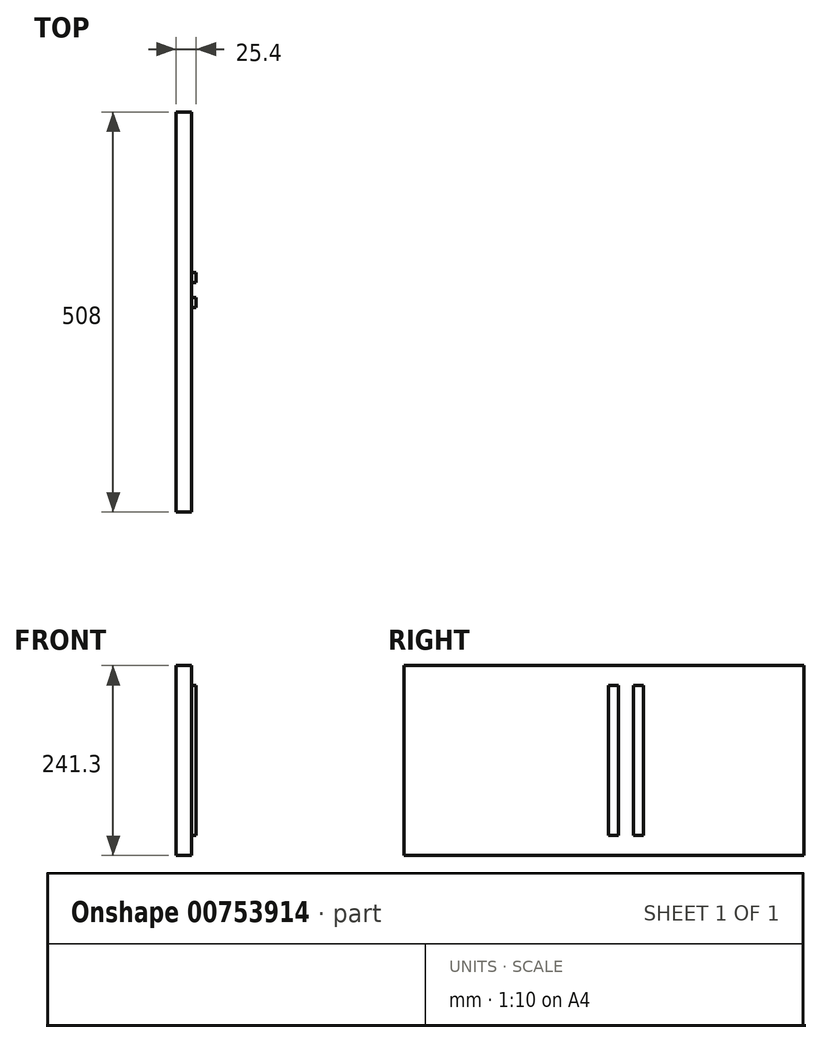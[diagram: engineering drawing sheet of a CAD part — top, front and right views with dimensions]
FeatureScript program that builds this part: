
annotation { "Feature Type Name" : "Feature", "Feature Type Description" : "" }
export const myFeature = defineFeature(function(context is Context, id is Id, definition is map)
    precondition{}
    {
        {
            var Q0;
            Q0=qCreatedBy(makeId("Right.planeOp"),FACE);
            var sketch = newSketch(context, id + "F0", { "sketchPlane" : qUnion([Q0])});
            skLineSegment(sketch, "E0.bottom", {"start": v(254, -120.65) * mm, "end": v(-254, -120.65) * mm});
            skLineSegment(sketch, "E0.top", {"start": v(254, 120.65) * mm, "end": v(-254, 120.65) * mm});
            skLineSegment(sketch, "E0.left", {"start": v(254, -120.65) * mm, "end": v(254, 120.65) * mm});
            skLineSegment(sketch, "E0.right", {"start": v(-254, -120.65) * mm, "end": v(-254, 120.65) * mm});
            skPoint(sketch, "E0.middle", {"position": v(0, 0) * mm});
            skLineSegment(sketch, "E1.0", {"start": v(253.65, 95.25) * mm, "end": v(-254, 95.25) * mm});
            skLineSegment(sketch, "E2.0", {"start": v(254, -95.25) * mm, "end": v(-254, -95.25) * mm});
            skLineSegment(sketch, "E3", {"start": v(253.65, 95.25) * mm, "end": v(50.45, 95.25) * mm});
            skLineSegment(sketch, "E4", {"start": v(50.45, 95.25) * mm, "end": v(37.75, 95.25) * mm});
            skLineSegment(sketch, "E5", {"start": v(37.75, 95.25) * mm, "end": v(18.7, 95.25) * mm});
            skLineSegment(sketch, "E6", {"start": v(18.7, 95.25) * mm, "end": v(6, 95.25) * mm});
            skLineSegment(sketch, "E7.bottom", {"start": v(6, 95.25) * mm, "end": v(18.7, 95.25) * mm});
            skLineSegment(sketch, "E7.top", {"start": v(6, -95.25) * mm, "end": v(18.7, -95.25) * mm});
            skLineSegment(sketch, "E7.left", {"start": v(6, 95.25) * mm, "end": v(6, -95.25) * mm});
            skLineSegment(sketch, "E7.right", {"start": v(18.7, 95.25) * mm, "end": v(18.7, -95.25) * mm});
            skLineSegment(sketch, "E8.bottom", {"start": v(37.75, 95.25) * mm, "end": v(50.45, 95.25) * mm});
            skLineSegment(sketch, "E8.top", {"start": v(37.75, -95.25) * mm, "end": v(50.45, -95.25) * mm});
            skLineSegment(sketch, "E8.left", {"start": v(37.75, 95.25) * mm, "end": v(37.75, -95.25) * mm});
            skLineSegment(sketch, "E8.right", {"start": v(50.45, 95.25) * mm, "end": v(50.45, -95.25) * mm});
            skSolve(sketch);
        }
        {
            var Q0;
            {var subQ0=sQuery(id+"F0.wireOp",EDGE,"E7.left");Q0=makeQuery(id+"F0.imprint","IMPRINT",FACE,{"disambiguationData":[TD([[makeQuery(id+"F0.imprint","IMPRINT",EDGE,{"derivedFrom":subQ0}),1.0]])]});}
            var Q1;
            {var subQ0=sQuery(id+"F0.wireOp",EDGE,"E8.left");Q1=makeQuery(id+"F0.imprint","IMPRINT",FACE,{"disambiguationData":[TD([[makeQuery(id+"F0.imprint","IMPRINT",EDGE,{"derivedFrom":subQ0}),1.0]])]});}
            extrude(context, id + "F1", {"entities" : qUnion([Q0, Q1]), "depth" : 6.35 * mm, "offsetDistance" : 25.4 * mm});
        }
        {
            var Q0;
            {var subQ5=sQuery(id+"F0.wireOp",EDGE,"E0.top");Q0=makeQuery(id+"F0.imprint","IMPRINT",FACE,{"disambiguationData":[TD([[makeQuery(id+"F0.imprint","IMPRINT",EDGE,{"derivedFrom":subQ5}),1.0]])]});}
            var Q1;
            {var subQ5=sQuery(id+"F0.wireOp",EDGE,"E7.left");Q1=makeQuery(id+"F0.imprint","IMPRINT",FACE,{"disambiguationData":[TD([[makeQuery(id+"F0.imprint","IMPRINT",EDGE,{"derivedFrom":subQ5}),-1.0]])]});}
            var Q2;
            {var subQ4=sQuery(id+"F0.wireOp",EDGE,"E0.bottom");Q2=makeQuery(id+"F0.imprint","IMPRINT",FACE,{"disambiguationData":[TD([[makeQuery(id+"F0.imprint","IMPRINT",EDGE,{"derivedFrom":subQ4}),-1.0]])]});}
            var Q3;
            {var subQ0=sQuery(id+"F0.wireOp",EDGE,"E7.left");Q3=makeQuery(id+"F0.imprint","IMPRINT",FACE,{"disambiguationData":[TD([[makeQuery(id+"F0.imprint","IMPRINT",EDGE,{"derivedFrom":subQ0}),1.0]])]});}
            var Q4;
            {var subQ2=sQuery(id+"F0.wireOp",EDGE,"E7.right");Q4=makeQuery(id+"F0.imprint","IMPRINT",FACE,{"disambiguationData":[TD([[makeQuery(id+"F0.imprint","IMPRINT",EDGE,{"derivedFrom":subQ2}),1.0]])]});}
            var Q5;
            {var subQ0=sQuery(id+"F0.wireOp",EDGE,"E8.left");Q5=makeQuery(id+"F0.imprint","IMPRINT",FACE,{"disambiguationData":[TD([[makeQuery(id+"F0.imprint","IMPRINT",EDGE,{"derivedFrom":subQ0}),1.0]])]});}
            extrude(context, id + "F2", {"entities" : qUnion([Q0, Q1, Q2, Q3, Q4, Q5]), "oppositeDirection" : true, "depth" : 19.05 * mm, "offsetDistance" : 25.4 * mm});
        }
    });
